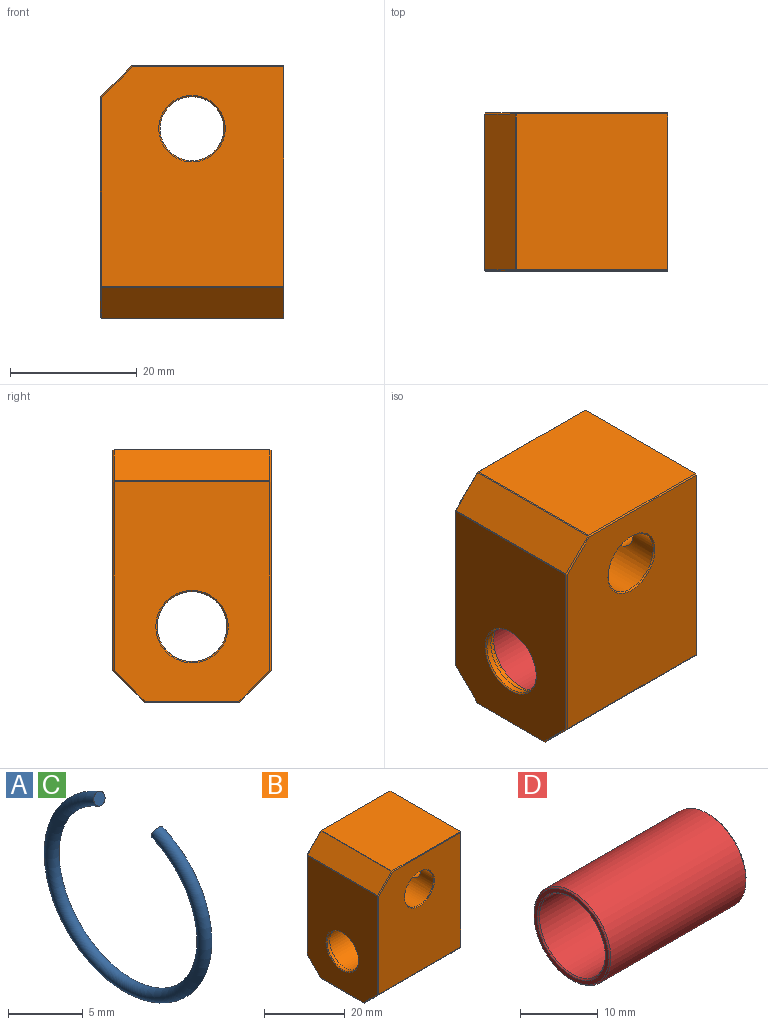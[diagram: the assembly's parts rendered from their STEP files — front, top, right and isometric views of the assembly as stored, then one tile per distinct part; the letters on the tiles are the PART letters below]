
ASSEMBLY  parts=4 mates=1
PART A: 3 faces, bbox 1x16.8x16.2 mm
  f0: torus R=7.25mm, axis (-1,0,0), area 125.6mm2, adj f1,f2
  f1: plane 1x0.93mm, normal (0,0.93,0.37), area 0.8mm2, adj f0
  f2: plane 1x0.93mm, normal (0,-0.93,0.37), area 0.8mm2, adj f0
PART B: 47 faces, bbox 29x25x40 mm
  f0: plane 34.72x24.6mm, normal (-1,0,0), area 727.4mm2, adj f25,f26,f34,f35,f39,f40,f44
  f1: plane 34.72x28.8mm, normal (0,-1,0), area 901.3mm2, adj f2,f19,f29,f36,f40,f42
  f2: plane 40x25mm, normal (1,0,0), area 794.7mm2, adj f1,f3,f4,f5,f9,f10,f12,f20
  f3: plane 34.72x28.8mm, normal (0,1,0), area 901.3mm2, adj f2,f20,f21,f26,f27,f43
  f4: plane 24.6x23.92mm, normal (0,0,1), area 588.4mm2, adj f2,f21,f28,f29
  f5: plane 28.8x14.83mm, normal (0,0,-1), area 427.2mm2, adj f2,f24,f33,f34
  f6: cylinder r=2.25mm len=8.98mm, axis (1,0,0), area 123.2mm2, adj f8,f45
  f7: cylinder r=2.25mm len=8.98mm, axis (1,0,0), area 123.2mm2, adj f8,f46
  f8: cylinder r=5.05mm len=24.6mm, axis (0,-1,0), area 747.9mm2, adj f6,f7,f19,f43
  f9: plane 28.8x4.88mm, normal (0,0.71,-0.71), area 198.9mm2, adj f2,f20,f24,f25
  f10: plane 28.8x4.88mm, normal (0,-0.71,-0.71), area 198.9mm2, adj f2,f33,f39,f42
  f11: plane 24.6x4.88mm, normal (-0.71,0,0.71), area 169.9mm2, adj f27,f28,f35,f36
  f12: cylinder r=6.02mm len=12.04mm, axis (-1,0,0), area 41.6mm2, adj f2,f13
  f13: plane 13.04x13.04mm, normal (-1,0,0), area 19.7mm2, adj f12,f14
  f14: cylinder r=6.52mm len=13.04mm, axis (-1,0,0), area 42.6mm2, adj f13,f15
  f15: plane 13.04x13.04mm, normal (1,0,0), area 19.7mm2, adj f14,f16
  f16: cylinder r=6.02mm len=25.76mm, axis (-1,0,0), area 974.4mm2, adj f15,f17
  f17: plane 12.04x12.04mm, normal (1,0,0), area 18.1mm2, adj f16,f18
  f18: cylinder r=5.52mm len=11.04mm, axis (-1,0,0), area 31.2mm2, adj f17,f44
  f19: cone r=5.05mm half-angle=45deg, axis (0,-1,0), area 9.2mm2, adj f1,f8
  f20: plane 28.8x0.14mm, normal (0,0.92,-0.38), area 4.4mm2, adj f2,f3,f9,f22
  f21: plane 23.92x0.2mm, normal (0,0.71,0.71), area 6.8mm2, adj f2,f3,f4,f23
  f22: plane 0.2x0.2mm, normal (-0.68,0.68,-0.28), area 0mm2, adj f20,f25,f26
  f23: plane 0.2x0.2mm, normal (-0.28,0.68,0.68), area 0mm2, adj f21,f27,f28
  f24: plane 28.8x0.14mm, normal (0,0.38,-0.92), area 4.4mm2, adj f2,f5,f9,f30
  f25: plane 5.02x5.02mm, normal (-0.71,0.5,-0.5), area 2mm2, adj f0,f9,f22,f30
  f26: plane 29.83x0.2mm, normal (-0.71,0.71,0), area 8.4mm2, adj f0,f3,f22,f31
  f27: plane 5.02x5.02mm, normal (-0.5,0.71,0.5), area 2mm2, adj f3,f11,f23,f31
  f28: plane 24.6x0.14mm, normal (-0.38,0,0.92), area 3.8mm2, adj f4,f11,f23,f32
  f29: plane 23.92x0.2mm, normal (0,-0.71,0.71), area 6.8mm2, adj f1,f2,f4,f32
  f30: plane 0.2x0.2mm, normal (-0.68,0.28,-0.68), area 0mm2, adj f24,f25,f34
  f31: plane 0.2x0.2mm, normal (-0.68,0.68,0.28), area 0mm2, adj f26,f27,f35
  f32: plane 0.2x0.2mm, normal (-0.28,-0.68,0.68), area 0mm2, adj f28,f29,f36
  f33: plane 28.8x0.14mm, normal (0,-0.38,-0.92), area 4.4mm2, adj f2,f5,f10,f37
  f34: plane 14.83x0.2mm, normal (-0.71,0,-0.71), area 4.2mm2, adj f0,f5,f30,f37
  f35: plane 24.6x0.14mm, normal (-0.92,0,0.38), area 3.8mm2, adj f0,f11,f31,f38
  f36: plane 5.02x5.02mm, normal (-0.5,-0.71,0.5), area 2mm2, adj f1,f11,f32,f38
  f37: plane 0.2x0.2mm, normal (-0.68,-0.28,-0.68), area 0mm2, adj f33,f34,f39
  f38: plane 0.2x0.2mm, normal (-0.68,-0.68,0.28), area 0mm2, adj f35,f36,f40
  f39: plane 5.02x5.02mm, normal (-0.71,-0.5,-0.5), area 2mm2, adj f0,f10,f37,f41
  f40: plane 29.83x0.2mm, normal (-0.71,-0.71,0), area 8.4mm2, adj f0,f1,f38,f41
  f41: plane 0.2x0.2mm, normal (-0.68,-0.68,-0.28), area 0mm2, adj f39,f40,f42
  f42: plane 28.8x0.14mm, normal (0,-0.92,-0.38), area 4.4mm2, adj f1,f2,f10,f41
  f43: cone r=5.05mm half-angle=45deg, axis (0,1,0), area 9.2mm2, adj f3,f8
  f44: cone r=5.52mm half-angle=45deg, axis (-1,0,0), area 10mm2, adj f0,f18
  f45: cone r=2.25mm half-angle=45deg, axis (1,0,0), area 24.4mm2, adj f2,f6
  f46: cone r=2.25mm half-angle=45deg, axis (1,0,0), area 24.4mm2, adj f2,f7
PART C: same geometry as A
PART D: 8 faces, bbox 25x14x14 mm
  f0: cylinder r=6mm len=24.6mm, axis (-1,0,0), area 927.4mm2, adj f4,f5
  f1: cylinder r=7mm len=24.6mm, axis (-1,0,0), area 1082mm2, adj f6,f7
  f2: plane 13.6x13.6mm, normal (1,0,0), area 24.5mm2, adj f5,f6
  f3: plane 13.6x13.6mm, normal (-1,0,0), area 24.5mm2, adj f4,f7
  f4: cone r=6.2mm half-angle=45deg, axis (-1,0,0), area 10.8mm2, adj f0,f3
  f5: cone r=6mm half-angle=45deg, axis (1,0,0), area 10.8mm2, adj f0,f2
  f6: cone r=6.8mm half-angle=45deg, axis (-1,0,0), area 12.3mm2, adj f1,f2
  f7: cone r=7mm half-angle=45deg, axis (1,0,0), area 12.3mm2, adj f1,f3
PLACE A t=(-42.98,5.62,21.5)mm
PLACE B t=(-30.1,5.62,9.5)mm
PLACE C t=(-17.22,5.62,21.5)mm
PLACE D t=(-42.6,5.62,21.5)mm
MATE fastened C.f0 <-> B.f12  axis (-1,0,0) through (-17.22,5.62,21.5)mm
